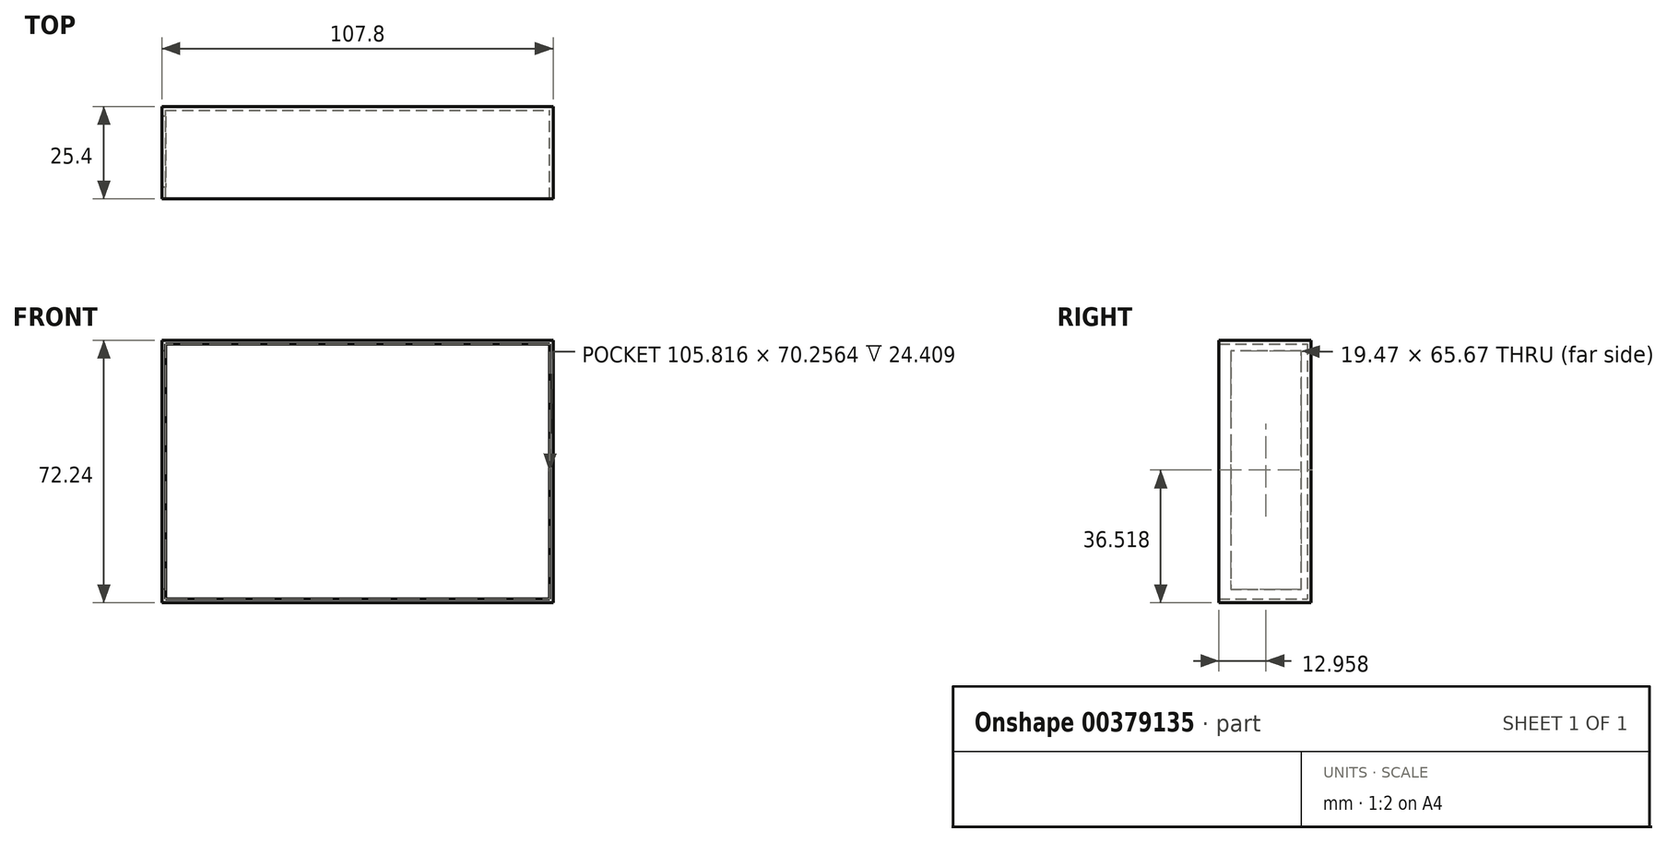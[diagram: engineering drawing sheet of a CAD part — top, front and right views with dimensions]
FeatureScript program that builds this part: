
annotation { "Feature Type Name" : "Feature", "Feature Type Description" : "" }
export const myFeature = defineFeature(function(context is Context, id is Id, definition is map)
    precondition{}
    {
        {
            var Q0;
            Q0=qCreatedBy(makeId("Front.planeOp"),FACE);
            var sketch = newSketch(context, id + "F0", { "sketchPlane" : qUnion([Q0])});
            skLineSegment(sketch, "E0.bottom", {"start": v(-53.9, 36.12) * mm, "end": v(53.9, 36.12) * mm});
            skLineSegment(sketch, "E0.top", {"start": v(-53.9, -36.12) * mm, "end": v(53.9, -36.12) * mm});
            skLineSegment(sketch, "E0.left", {"start": v(-53.9, 36.12) * mm, "end": v(-53.9, -36.12) * mm});
            skLineSegment(sketch, "E0.right", {"start": v(53.9, 36.12) * mm, "end": v(53.9, -36.12) * mm});
            skPoint(sketch, "E0.middle", {"position": v(0, 0) * mm});
            skSolve(sketch);
        }
        {
            var Q0;
            Q0=qSketchRegion(id+"F0",true);
            extrude(context, id + "F1", {"entities" : qUnion([Q0]), "depth" : 25.4 * mm});
        }
        {
            var Q0;
            Q0=makeQuery(id+"F1.opExtrude","CAP_FACE",FACE,{"disambiguationData":[OSD([sQuery(id+"F0.wireOp",EDGE,"E0.bottom"),sQuery(id+"F0.wireOp",EDGE,"E0.top"),sQuery(id+"F0.wireOp",EDGE,"E0.left"),sQuery(id+"F0.wireOp",EDGE,"E0.right")])],"isStart":false});
            shell(context, id + "F2", {"entities" : qUnion([Q0]), "thickness" : 1 * mm});
        }
        {
            var Q0;
            Q0=makeQuery(id+"F1.opExtrude","SWEPT_FACE",FACE,{"disambiguationData":[OSD([sQuery(id+"F0.wireOp",EDGE,"E0.left")])]});
            var sketch = newSketch(context, id + "F3", { "sketchPlane" : qUnion([Q0])});
            skLineSegment(sketch, "E1", {"start": v(22.18, 33.23) * mm, "end": v(22.18, -32.44) * mm});
            skLineSegment(sketch, "E2", {"start": v(22.18, -32.44) * mm, "end": v(2.7, -32.44) * mm});
            skLineSegment(sketch, "E3", {"start": v(2.7, -32.44) * mm, "end": v(2.7, 33.23) * mm});
            skLineSegment(sketch, "E4", {"start": v(2.7, 33.23) * mm, "end": v(22.18, 33.23) * mm});
            skSolve(sketch);
        }
        {
            var Q0;
            Q0=qSketchRegion(id+"F3",true);
            extrude(context, id + "F4", {"entities" : qUnion([Q0]), "operationType" : NewBodyOperationType.REMOVE, "oppositeDirection" : true, "depth" : 25.4 * mm});
        }
    });
